# Revit family: monsun_r__ex_51fxb2dp4b0a_6f7a
name_source: partatom
category: Lighting Fixtures
units: mm (PartAtom-declared; Revit-internal decimal feet)

## family parameters
Cut with Voids When Loaded = No
Host = Face
Light Source = No
Part Type = Normal
Room Calculation Point = No
Round Connector Dimension = Use Diameter
Shared = No

## types (1)
- Monsun® Ex (1 x LED, 13730 lm, 94.7 W, 4000K)
    Apparent Load = 95 VA
    CIE Flux Codes = 43 72 91 92 100
    Color Rendering = 80
    Color Temperature = 4000K
    Default Elevation = 1800 mm
    Description = Monsun® Ex, damp-proof luminaire, primary optical cover: cover, of PC, UV-stabilised, opal, light emission: direct distribution, primary light characteristic: symmetric, installation type: surface-mounted, LED, rated luminous flux: 13.730lm, luminous efficacy: 145lm/W, light colour: 840, colour temperature: 4000K, control gear: ECG DALI, with terminal, 5-pole, max. 2.5mm², through-wiring: 7x 2.5mm², mains connection: 220..240V, AC, 50/60Hz, rated input power: 95W, housing, of PC, light grey (RAL 7035), incl. blind plug, incl. 1x Ex cable gland M20 for cable diameter 7..12mm with sealing, length: 1.580mm, width: 155mm, height: 105mm, clip for enclosure, of stainless steel, protection rating (complete): IP66, insulation class (complete): insulation class I (protective earthing), certification: CE, explosion class: zone2,22 II 3G Ex nR IIC T6 GC, II 3D Ex tc IIIC T80°C Dc, impact resistance: IK10, permissible operating ambient temperature: -20..+40°C, LABS conformity tested according to VDMA 24364:2018-05, contact your sales advisor before using the luminaires in applications with unclear chemical exposure, large temperature fluctuations or condensation-forming humidity, packaging unit: 1 piece
    Height = 105 mm
    Lamp = 1 x LED
    Lamp Light Flux = 13730 lm
    Lamp Power = 94.7 W
    Lamp count = 1
    Length = 1580 mm
    Luminous efficacy = 145 lm/W
    Manufacturer = Siteco
    ModVariant = No
    Model = 51FXB2DP4B0A
    Mounting Place = Ceiling
    Mounting Type = Surface mounted
    Number of Poles = 1
    OnlyDefault = Yes
    Power Factor = 1
    Product Name = Monsun® Ex
    Product group = damp-proof luminaire
    ProductGroupID = 301
    Protection Class = Protection class I
    Protection Degree = IP 66
    RLX_Detail_Level = 1
    RLX_Emergency_Light_Flux = 0 lm
    RLX_Emergency_Type = 0
    RLX_Emergency_Type_DB = No
    RlxData = <blob elided: 42165 chars, md5=7462a74a>
    Socket = socket
    Standby Power = 0 W
    System Light Flux = 13730 lm
    System Power = 95 W
    Type Comments = Product without accessories
    Type Image = l_1258882.jpg
    URL = http://relux.com
    VarID = ---
    Voltage = 0 V
    Weight = 0.00 kg
    Width = 155 mm

## geometry (parser evidence)
native form markers: Sweep x13
no freeform markers — native parametric forms only
